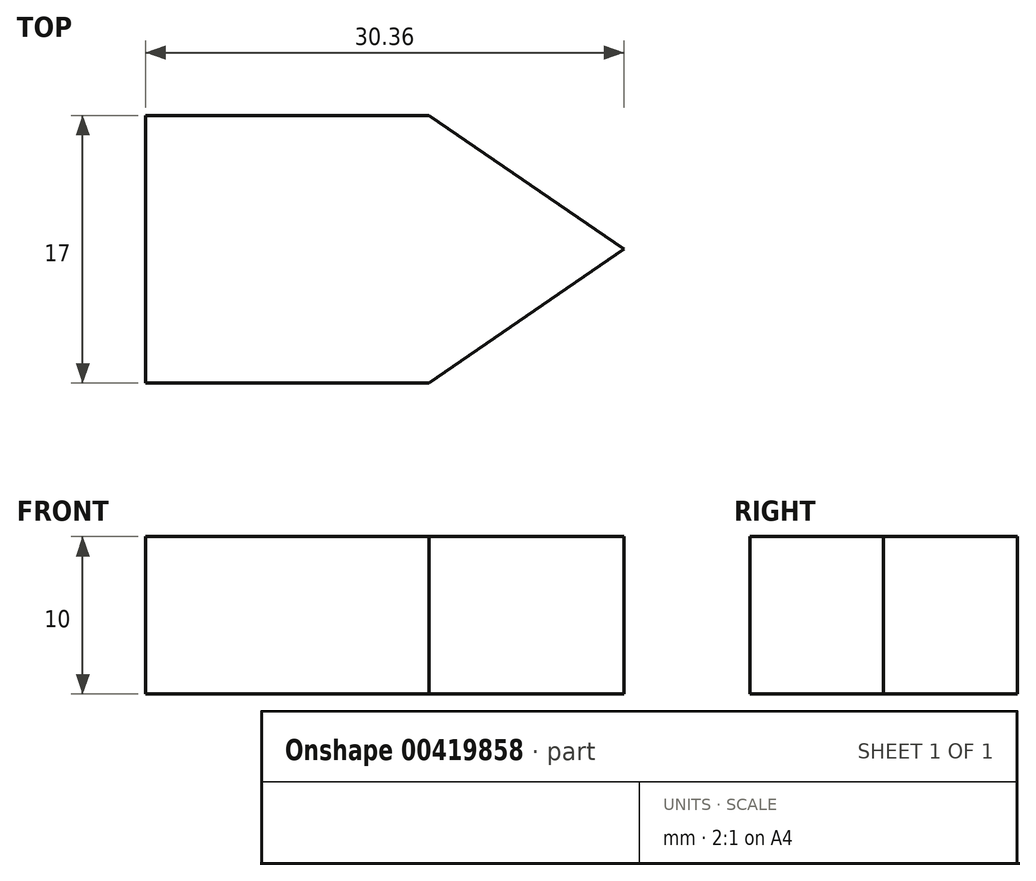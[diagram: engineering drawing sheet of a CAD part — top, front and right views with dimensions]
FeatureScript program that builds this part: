
annotation { "Feature Type Name" : "Feature", "Feature Type Description" : "" }
export const myFeature = defineFeature(function(context is Context, id is Id, definition is map)
    precondition{}
    {
        {
            var Q0;
            Q0=qCreatedBy(makeId("Top.planeOp"),FACE);
            var sketch = newSketch(context, id + "F0", { "sketchPlane" : qUnion([Q0])});
            skLineSegment(sketch, "E0.bottom", {"start": v(-64.58, 47.36) * mm, "end": v(-46.58, 47.36) * mm});
            skLineSegment(sketch, "E0.top", {"start": v(-64.58, 30.36) * mm, "end": v(-46.58, 30.36) * mm});
            skLineSegment(sketch, "E0.left", {"start": v(-64.58, 47.36) * mm, "end": v(-64.58, 30.36) * mm});
            skLineSegment(sketch, "E0.right", {"start": v(-46.58, 47.36) * mm, "end": v(-46.58, 30.36) * mm});
            skLineSegment(sketch, "E1", {"start": v(-46.58, 47.36) * mm, "end": v(-34.22, 38.86) * mm});
            skLineSegment(sketch, "E2", {"start": v(-34.22, 38.86) * mm, "end": v(-46.58, 30.36) * mm});
            skSolve(sketch);
        }
        {
            var Q0;
            Q0 = qSketchRegion(id + "F0", true);
            extrude(context, id + "F1", {"entities" : qUnion([Q0]), "depth" : 10 * mm});
        }
    });
